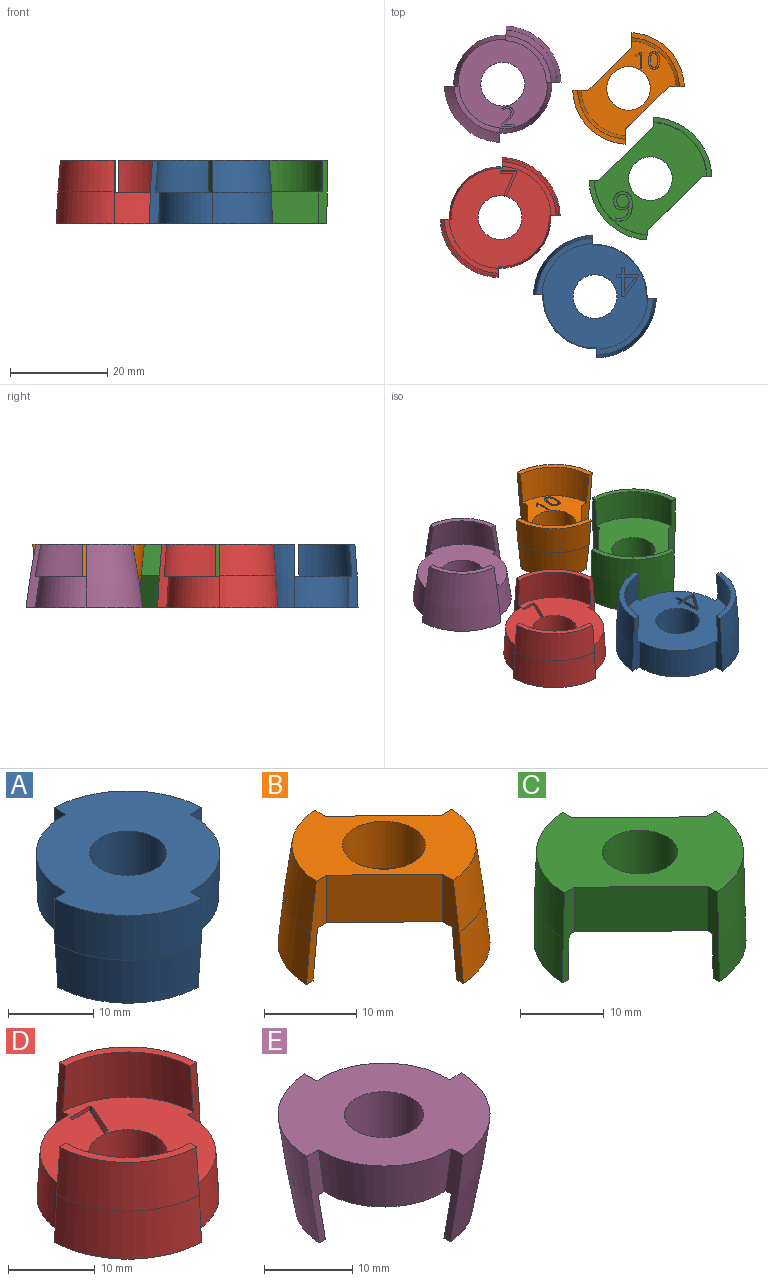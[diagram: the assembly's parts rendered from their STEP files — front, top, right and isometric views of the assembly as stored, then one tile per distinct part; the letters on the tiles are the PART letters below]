
ASSEMBLY  parts=5 mates=4
PART A: 35 faces, bbox 25.6x25.6x13.3 mm
  f0: plane 22.79x22.79mm, normal (0,0,-1), area 303.7mm2, adj f1,f2,f4,f8,f9,f11,f13,f14
  f1: revolved ~11.15x11.15mm, area 114.5mm2, adj f0,f3,f9,f13
  f2: revolved ~11.15x11.15mm, area 114.5mm2, adj f0,f3,f8,f14
  f3: plane 25.29x25.29mm, normal (0,0,1), area 366.2mm2, adj f1,f2,f5,f8,f9,f10,f13,f14
  f4: revolved ~11.01x11.01mm, area 109.3mm2, adj f0,f7,f8,f9
  f5: revolved ~12.25x12.25mm, area 123.5mm2, adj f3,f6,f8,f9
  f6: revolved ~12.11x12.11mm, area 120.6mm2, adj f5,f7,f8,f9
  f7: plane 11.6x11.6mm, normal (0,0,-1), area 19mm2, adj f4,f6,f8,f9
  f8: plane 13.31x2.36mm, normal (1,0,0), area 19.5mm2, adj f0,f2,f3,f4,f5,f6,f7
  f9: plane 13.31x2.36mm, normal (0,1,0), area 19.5mm2, adj f0,f1,f3,f4,f5,f6,f7
  f10: revolved ~13x12.26mm, area 244.1mm2, adj f3,f12,f13,f14
  f11: revolved ~11.01x11.01mm, area 109.3mm2, adj f0,f12,f13,f14
  f12: plane 11.6x11.6mm, normal (0,0,-1), area 19mm2, adj f10,f11,f13,f14
  f13: plane 13.32x2.37mm, normal (-1,0,0), area 19.5mm2, adj f0,f1,f3,f10,f11,f12
  f14: plane 13.32x2.36mm, normal (0,-1,0), area 19.5mm2, adj f0,f2,f3,f10,f11,f12
  f15: cylinder r=4.5mm len=9mm, axis (0,0,1), area 183.8mm2, adj f0,f3
  f16: plane 5x1.98mm, normal (1,0,0), area 9.9mm2, adj f17,f32,f33,f34
  f17: plane 5x2.22mm, normal (0,1,0), area 11.1mm2, adj f16,f18,f33,f34
  f18: plane 5x2.64mm, normal (-0.82,-0.58,0), area 16.2mm2, adj f17,f19,f33,f34
  f19: extruded ~5x0.65mm, area 3.7mm2, adj f18,f20,f33,f34
  f20: plane 5x0.03mm, normal (0,-1,0), area 0.2mm2, adj f19,f32,f33,f34
  f21: plane 5x0.88mm, normal (0,-1,0), area 4.4mm2, adj f0,f22,f31,f33
  f22: plane 5x0.61mm, normal (-1,0,0), area 3.1mm2, adj f0,f21,f23,f33
  f23: plane 5x0.88mm, normal (0,1,0), area 4.4mm2, adj f0,f22,f24,f33
  f24: plane 5x4mm, normal (-1,0,0), area 20mm2, adj f0,f23,f25,f33
  f25: plane 5x0.72mm, normal (0,1,0), area 3.6mm2, adj f0,f24,f26,f33
  f26: plane 5x4.02mm, normal (0.82,0.57,0), area 24.6mm2, adj f0,f25,f27,f33
  f27: plane 5x0.59mm, normal (1,0,0), area 2.9mm2, adj f0,f26,f28,f33
  f28: plane 5x2.89mm, normal (0,-1,0), area 14.5mm2, adj f0,f27,f29,f33
  f29: plane 5x1.37mm, normal (1,0,0), area 6.8mm2, adj f0,f28,f30,f33
  f30: plane 5x0.65mm, normal (0,-1,0), area 3.2mm2, adj f0,f29,f31,f33
  f31: plane 5x1.37mm, normal (-1,0,0), area 6.8mm2, adj f0,f21,f30,f33
  f32: extruded ~5x1.31mm, area 6.6mm2, adj f16,f20,f33,f34
  f33: plane 5.98x4.42mm, normal (0,0,-1), area 8.5mm2, adj f16,f17,f18,f19,f20,f21,f22,f23
  f34: plane 3.29x2.26mm, normal (0,0,-1), area 3.5mm2, adj f16,f17,f18,f19,f20,f32
PART B: 45 faces, bbox 23.1x23.1x13.1 mm
  f0: plane 19.63x19.6mm, normal (0,0,-1), area 137.3mm2, adj f5,f6,f7,f8,f12,f13,f14,f15
  f1: plane 19.98x19.96mm, normal (0,0,1), area 151mm2, adj f2,f6,f7,f11,f12,f13,f14,f15
  f2: revolved ~10.46x10.22mm, area 100.5mm2, adj f1,f3,f6,f7
  f3: revolved ~11.11x10.84mm, area 107.7mm2, adj f2,f4,f6,f7
  f4: plane 11.08x10.82mm, normal (0,0,-1), area 16.3mm2, adj f3,f5,f6,f7
  f5: revolved ~10.11x9.86mm, area 100.5mm2, adj f0,f4,f6,f7
  f6: plane 13.13x3.27mm, normal (1,0.03,0), area 19.8mm2, adj f0,f1,f2,f3,f4,f5,f15
  f7: plane 13.13x3.27mm, normal (0,-1,0), area 19.8mm2, adj f0,f1,f2,f3,f4,f5,f14
  f8: revolved ~10.11x9.86mm, area 100.5mm2, adj f0,f9,f12,f13
  f9: plane 11.08x10.82mm, normal (0,0,-1), area 16.3mm2, adj f8,f10,f12,f13
  f10: revolved ~11.11x10.84mm, area 107.7mm2, adj f9,f11,f12,f13
  f11: revolved ~10.46x10.22mm, area 100.5mm2, adj f1,f10,f12,f13
  f12: plane 13.13x3.27mm, normal (-1,-0.03,0), area 19.8mm2, adj f0,f1,f8,f9,f10,f11,f14
  f13: plane 13.13x3.27mm, normal (0,1,0), area 19.8mm2, adj f0,f1,f8,f9,f10,f11,f15
  f14: plane 8.97x8.74mm, normal (-0.7,-0.72,0), area 78.9mm2, adj f0,f1,f7,f12
  f15: plane 8.97x8.74mm, normal (0.7,0.72,0), area 78.9mm2, adj f0,f1,f6,f13
  f16: cylinder r=4.5mm len=9mm, axis (0,0,1), area 178.1mm2, adj f0,f1
  f17: extruded ~5x1.1mm, area 5.6mm2, adj f18,f32,f33,f44
  f18: extruded ~5x1.1mm, area 5.6mm2, adj f17,f19,f33,f44
  f19: extruded ~5x0.57mm, area 3.5mm2, adj f18,f20,f33,f44
  f20: extruded ~5x0.57mm, area 3.5mm2, adj f19,f21,f33,f44
  f21: extruded ~5x1.1mm, area 5.6mm2, adj f20,f22,f33,f44
  f22: extruded ~5x1.1mm, area 5.6mm2, adj f21,f23,f33,f44
  f23: extruded ~5x0.57mm, area 3.5mm2, adj f22,f32,f33,f44
  f24: extruded ~5x1.34mm, area 7mm2, adj f0,f25,f31,f33
  f25: extruded ~5x1.33mm, area 6.9mm2, adj f0,f24,f26,f33
  f26: extruded ~5x0.86mm, area 5.1mm2, adj f0,f25,f27,f33
  f27: extruded ~5x0.86mm, area 5.1mm2, adj f0,f26,f28,f33
  f28: extruded ~5x1.35mm, area 7mm2, adj f0,f27,f29,f33
  f29: extruded ~5x1.33mm, area 6.9mm2, adj f0,f28,f30,f33
  f30: extruded ~5x0.85mm, area 5.1mm2, adj f0,f29,f31,f33
  f31: extruded ~5x0.87mm, area 5.1mm2, adj f0,f24,f30,f33
  f32: extruded ~5x0.57mm, area 3.5mm2, adj f17,f23,f33,f44
  f33: plane 3.57x2.3mm, normal (0,0,-1), area 3.2mm2, adj f17,f18,f19,f20,f21,f22,f23,f24
  f34: plane 5x0.38mm, normal (0,-1,0), area 1.9mm2, adj f0,f35,f42,f43
  f35: plane 5x3.47mm, normal (-1,0,0), area 17.4mm2, adj f0,f34,f36,f43
  f36: plane 5x0.33mm, normal (0,1,0), area 1.7mm2, adj f0,f35,f37,f43
  f37: plane 5x0.92mm, normal (0.61,0.79,0), area 5.8mm2, adj f0,f36,f38,f43
  f38: plane 5x0.27mm, normal (0.79,-0.61,0), area 1.7mm2, adj f0,f37,f39,f43
  f39: extruded ~5x0.56mm, area 3.7mm2, adj f0,f38,f40,f43
  f40: extruded ~5x0.11mm, area 0.8mm2, adj f0,f39,f41,f43
  f41: extruded ~5x0.58mm, area 2.9mm2, adj f0,f40,f42,f43
  f42: plane 5x2.47mm, normal (1,0,0), area 12.4mm2, adj f0,f34,f41,f43
  f43: plane 3.47x1.25mm, normal (0,0,-1), area 1.6mm2, adj f34,f35,f36,f37,f38,f39,f40,f41
  f44: plane 2.89x1.49mm, normal (0,0,-1), area 3.6mm2, adj f17,f18,f19,f20,f21,f22,f23,f32
PART C: 43 faces, bbox 25.5x25.4x13.2 mm
  f0: plane 23.15x23.12mm, normal (0,0,-1), area 233mm2, adj f2,f6,f7,f8,f11,f12,f13,f14
  f1: plane 24.71x24.68mm, normal (0,0,1), area 275.2mm2, adj f3,f6,f7,f10,f11,f12,f13,f14
  f2: revolved ~11.23x10.94mm, area 111.6mm2, adj f0,f5,f6,f7
  f3: revolved ~12.17x11.86mm, area 120.2mm2, adj f1,f4,f6,f7
  f4: revolved ~12.23x11.92mm, area 121.6mm2, adj f3,f5,f6,f7
  f5: plane 12.23x11.94mm, normal (0,0,-1), area 18mm2, adj f2,f4,f6,f7
  f6: plane 13.16x2.11mm, normal (1,0.03,0), area 18.1mm2, adj f0,f1,f2,f3,f4,f5,f14
  f7: plane 13.16x2.11mm, normal (0,-1,0), area 18.1mm2, adj f0,f1,f2,f3,f4,f5,f13
  f8: revolved ~11.23x10.94mm, area 111.6mm2, adj f0,f9,f11,f12
  f9: plane 12.23x11.94mm, normal (0,0,-1), area 18mm2, adj f8,f10,f11,f12
  f10: revolved ~13x12.24mm, area 241.8mm2, adj f1,f9,f11,f12
  f11: plane 13.16x2.11mm, normal (-1,-0.03,0), area 18.1mm2, adj f0,f1,f8,f9,f10,f13
  f12: plane 13.16x2.11mm, normal (0,1,0), area 18.1mm2, adj f0,f1,f8,f9,f10,f14
  f13: plane 11.38x11.08mm, normal (-0.7,-0.72,0), area 103.2mm2, adj f0,f1,f7,f11
  f14: plane 11.38x11.08mm, normal (0.7,0.72,0), area 103.2mm2, adj f0,f1,f6,f12
  f15: cylinder r=4.5mm len=9mm, axis (0,0,1), area 183.8mm2, adj f0,f1
  f16: extruded ~5x0.9mm, area 5mm2, adj f17,f40,f41,f42
  f17: extruded ~5x0.68mm, area 3.6mm2, adj f16,f18,f41,f42
  f18: extruded ~5x0.57mm, area 3.7mm2, adj f17,f19,f41,f42
  f19: extruded ~5x0.78mm, area 4mm2, adj f18,f20,f41,f42
  f20: extruded ~5x0.55mm, area 2.9mm2, adj f19,f21,f41,f42
  f21: extruded ~5x0.49mm, area 3.2mm2, adj f20,f22,f41,f42
  f22: extruded ~5x0.67mm, area 3.5mm2, adj f21,f23,f41,f42
  f23: extruded ~5x0.89mm, area 4.9mm2, adj f22,f24,f41,f42
  f24: extruded ~5x0.93mm, area 5mm2, adj f23,f40,f41,f42
  f25: extruded ~5x2.62mm, area 13.8mm2, adj f0,f26,f39,f41
  f26: extruded ~5x1.93mm, area 10.2mm2, adj f0,f25,f27,f41
  f27: extruded ~5x1.46mm, area 8.4mm2, adj f0,f26,f28,f41
  f28: extruded ~5x1.37mm, area 7.6mm2, adj f0,f27,f29,f41
  f29: extruded ~5x1.46mm, area 7.9mm2, adj f0,f28,f30,f41
  f30: extruded ~5x1.31mm, area 7.1mm2, adj f0,f29,f31,f41
  f31: extruded ~5x1.26mm, area 7mm2, adj f0,f30,f32,f41
  f32: extruded ~5x1.42mm, area 8.3mm2, adj f0,f31,f33,f41
  f33: plane 5x0.05mm, normal (0,1,0), area 0.2mm2, adj f0,f32,f34,f41
  f34: extruded ~5x1.87mm, area 9.9mm2, adj f0,f33,f35,f41
  f35: extruded ~5x1.46mm, area 8.2mm2, adj f0,f34,f36,f41
  f36: extruded ~5x0.72mm, area 3.6mm2, adj f0,f35,f37,f41
  f37: plane 5x0.58mm, normal (-1,0,0), area 2.9mm2, adj f0,f36,f38,f41
  f38: extruded ~5x0.72mm, area 3.7mm2, adj f0,f37,f39,f41
  f39: extruded ~5x2.02mm, area 11.4mm2, adj f0,f25,f38,f41
  f40: extruded ~5x1.05mm, area 5.6mm2, adj f16,f24,f41,f42
  f41: plane 6.12x3.88mm, normal (0,0,-1), area 9.2mm2, adj f16,f17,f18,f19,f20,f21,f22,f23
  f42: plane 2.68x2.52mm, normal (0,0,-1), area 5.5mm2, adj f16,f17,f18,f19,f20,f21,f22,f23
PART D: 25 faces, bbox 24.7x24.7x13 mm
  f0: plane 22.01x22.01mm, normal (0,0,1), area 281.7mm2, adj f1,f2,f4,f8,f9,f12,f14,f15
  f1: revolved ~10.87x10.87mm, area 107.1mm2, adj f0,f3,f9,f14
  f2: revolved ~10.87x10.87mm, area 107.1mm2, adj f0,f3,f8,f15
  f3: plane 24.71x24.71mm, normal (0,0,-1), area 345.2mm2, adj f1,f2,f7,f8,f9,f13,f14,f15
  f4: revolved ~10.63x10.63mm, area 108.3mm2, adj f0,f5,f8,f9
  f5: plane 11.1x11.1mm, normal (0,0,1), area 16.5mm2, adj f4,f6,f8,f9
  f6: revolved ~11.61x11.61mm, area 115.3mm2, adj f5,f7,f8,f9
  f7: revolved ~11.97x11.97mm, area 119.5mm2, adj f3,f6,f8,f9
  f8: plane 13.03x2.28mm, normal (1,0,0), area 18.7mm2, adj f0,f2,f3,f4,f5,f6,f7
  f9: plane 13.03x2.28mm, normal (0,1,0), area 18.7mm2, adj f0,f1,f3,f4,f5,f6,f7
  f10: revolved ~11.61x11.61mm, area 115.3mm2, adj f11,f13,f14,f15
  f11: plane 11.1x11.1mm, normal (0,0,1), area 16.5mm2, adj f10,f12,f14,f15
  f12: revolved ~10.63x10.63mm, area 108.3mm2, adj f0,f11,f14,f15
  f13: revolved ~11.97x11.97mm, area 119.5mm2, adj f3,f10,f14,f15
  f14: plane 13.03x2.28mm, normal (-1,0,0), area 18.7mm2, adj f0,f1,f3,f10,f11,f12,f13
  f15: plane 13.03x2.28mm, normal (0,-1,0), area 18.7mm2, adj f0,f2,f3,f10,f11,f12,f13
  f16: cylinder r=4.5mm len=9mm, axis (0,0,1), area 178.1mm2, adj f0,f3
  f17: plane 5x4.44mm, normal (0.91,-0.42,0), area 24.5mm2, adj f0,f18,f23,f24
  f18: plane 5x0.62mm, normal (0,1,0), area 3.1mm2, adj f0,f17,f19,f24
  f19: plane 5x4.51mm, normal (-0.91,0.41,0), area 24.7mm2, adj f0,f18,f20,f24
  f20: plane 5x0.45mm, normal (-1,0,0), area 2.3mm2, adj f0,f19,f21,f24
  f21: plane 5x3.3mm, normal (0,-1,0), area 16.5mm2, adj f0,f20,f22,f24
  f22: plane 5x0.52mm, normal (1,0,0), area 2.6mm2, adj f0,f21,f23,f24
  f23: plane 5x2.7mm, normal (0,1,0), area 13.5mm2, adj f0,f17,f22,f24
  f24: plane 4.96x3.3mm, normal (0,0,1), area 4.4mm2, adj f17,f18,f19,f20,f21,f22,f23
PART E: 37 faces, bbox 24.9x24.8x13.9 mm
  f0: plane 20.25x20.23mm, normal (0,0,-1), area 225.9mm2, adj f1,f2,f4,f8,f9,f10,f13,f14
  f1: revolved ~10.8x10.54mm, area 103.5mm2, adj f0,f3,f8,f14
  f2: revolved ~10.8x10.54mm, area 103.5mm2, adj f0,f3,f9,f13
  f3: plane 24.01x23.98mm, normal (0,0,1), area 319mm2, adj f1,f2,f5,f8,f9,f12,f13,f14
  f4: revolved ~9.76x9.54mm, area 95mm2, adj f0,f7,f8,f9
  f5: revolved ~11.62x11.34mm, area 112.2mm2, adj f3,f6,f8,f9
  f6: revolved ~10.73x10.49mm, area 102.3mm2, adj f5,f7,f8,f9
  f7: plane 9.58x9.36mm, normal (0,0,-1), area 14.1mm2, adj f4,f6,f8,f9
  f8: plane 13.34x3.37mm, normal (1,0.03,0), area 18.9mm2, adj f0,f1,f3,f4,f5,f6,f7
  f9: plane 13.34x3.37mm, normal (0,-1,0), area 18.9mm2, adj f0,f2,f3,f4,f5,f6,f7
  f10: revolved ~9.76x9.54mm, area 95mm2, adj f0,f11,f13,f14
  f11: plane 9.58x9.36mm, normal (0,0,-1), area 14.1mm2, adj f10,f12,f13,f14
  f12: revolved ~13x11.66mm, area 214.4mm2, adj f3,f11,f13,f14
  f13: plane 13.85x3.88mm, normal (-1,-0.03,0), area 18.9mm2, adj f0,f2,f3,f10,f11,f12
  f14: plane 13.85x3.88mm, normal (0,1,0), area 18.9mm2, adj f0,f1,f3,f10,f11,f12
  f15: cylinder r=4.5mm len=9mm, axis (0,0,1), area 178.1mm2, adj f0,f3
  f16: plane 4.8x0.42mm, normal (1,0,0), area 2mm2, adj f0,f17,f35,f36
  f17: plane 4.8x2.61mm, normal (0,1,0), area 12.5mm2, adj f0,f16,f18,f36
  f18: plane 4.8x0.39mm, normal (-1,0,0), area 1.9mm2, adj f0,f17,f19,f36
  f19: plane 4.8x1.05mm, normal (-0.71,-0.71,0), area 7.1mm2, adj f0,f18,f20,f36
  f20: extruded ~4.8x0.69mm, area 4.5mm2, adj f0,f19,f21,f36
  f21: extruded ~4.8x0.4mm, area 2.2mm2, adj f0,f20,f22,f36
  f22: extruded ~4.8x0.42mm, area 2.1mm2, adj f0,f21,f23,f36
  f23: extruded ~4.8x0.5mm, area 2.7mm2, adj f0,f22,f24,f36
  f24: extruded ~4.8x0.53mm, area 2.8mm2, adj f0,f23,f25,f36
  f25: extruded ~4.8x0.47mm, area 2.3mm2, adj f0,f24,f26,f36
  f26: extruded ~4.8x0.49mm, area 2.8mm2, adj f0,f25,f27,f36
  f27: plane 4.8x0.31mm, normal (-0.79,0.61,0), area 1.9mm2, adj f0,f26,f28,f36
  f28: extruded ~4.8x1.19mm, area 6.3mm2, adj f0,f27,f29,f36
  f29: extruded ~4.8x0.88mm, area 4.5mm2, adj f0,f28,f30,f36
  f30: extruded ~4.8x0.77mm, area 4.1mm2, adj f0,f29,f31,f36
  f31: extruded ~4.8x0.75mm, area 3.8mm2, adj f0,f30,f32,f36
  f32: extruded ~4.8x0.93mm, area 5.9mm2, adj f0,f31,f33,f36
  f33: plane 4.8x0.87mm, normal (0.7,0.71,0), area 5.8mm2, adj f0,f32,f34,f36
  f34: plane 4.8x0.02mm, normal (1,0,0), area 0.1mm2, adj f0,f33,f35,f36
  f35: plane 4.8x2.04mm, normal (0,-1,0), area 9.8mm2, adj f0,f16,f34,f36
  f36: plane 4.02x2.61mm, normal (0,0,-1), area 3.5mm2, adj f16,f17,f18,f19,f20,f21,f22,f23
PLACE A rot(axis=(0,1,0),180deg) t=(14.09,-43.7,46.99)mm
PLACE B rot(axis=(1,0,0),180deg) t=(21.01,-0.84,85.99)mm
PLACE C rot(axis=(0,1,0),180deg) t=(25.52,-19.41,59.99)mm
PLACE D t=(-5.42,-27.42,-18.01)mm
PLACE E rot(axis=(0,1,0),180deg) t=(-4.89,0.04,33.99)mm fixed
MATE planar B.f16 <-> E.f15  axis (0,0,-1) through (21.01,-0.84,20.99)mm
MATE planar D.f16 <-> E.f15  axis (0,0,-1) through (-5.42,-27.42,20.99)mm
MATE planar E.f15 <-> A.f15  axis (0,0,-1) through (-4.89,0.04,20.99)mm
MATE planar E.f15 <-> C.f15  axis (0,0,-1) through (-4.89,0.04,20.99)mm
